# Revit family: 01-70-035-DN100-150
name_source: partatom
category: Pipe Accessories
units: mm (PartAtom-declared; Revit-internal decimal feet)

## family parameters
Always vertical = No
Cut with Voids When Loaded = No
Part Type = Valve - Breaks Into
Round Connector Dimension = Use Diameter
Shared = No
Work Plane-Based = No

## types (5) — shared parameters
Body_Wallthickness = 10 mm  [stored 0.0328084 ft]
Body_Wallthickness_1 = 20 mm  [stored 0.0656168 ft]
Body_Wallthickness_2 = 5 mm  [stored 0.0164042 ft]
Bonnet_Flange_cut = 8 mm  [stored 0.0262467 ft]
Bonnet_Flange_thickness = 15 mm  [stored 0.0492126 ft]
D = 63 mm  [stored 0.206693 ft]
D1 = 10 mm  [stored 0.0328084 ft]
D2 = 34 mm  [stored 0.111549 ft]
DN100_PN16 = 01-110-70-0146499
DN125_PN 16 = 01-140-70-0146499
DN125_PN16 = 01-125-70-0146499
DN150_PN 16 = 01-160-70-0146499
DN150_PN16 = 01-180-70-0146499
Description_ = AVK GATE VALVE, SUPA PLUS™
E = 15 mm  [stored 0.0492126 ft]
F = 10 mm  [stored 0.0328084 ft]
F1 = 22 mm  [stored 0.0721785 ft]
Flange_Thickness = 19 mm  [stored 0.062336 ft]
Flange_width = 30 mm  [stored 0.0984252 ft]
Ftc = 4 mm  [stored 0.0131234 ft]
Name_Height_reference = 10 mm  [stored 0.0328084 ft]
Rib_Height_Reference_1 = 120 mm
Rib_Height_Reference_2 = 110 mm
Rib_Height_Reference_3 = 100 mm
Rib_Thickness = 18 mm  [stored 0.0590551 ft]
Search_table = 01-70-035-DN100-150
URL product pages = https://www.avkvalves.com
zero-valued in all types: Bottom_Reference

## per-type parameters (varying)
- DN100_PN16: At=83 mm; Body_Height=122 mm; Body_depth=166 mm; Body_width=80 mm  [stored 0.262467 ft]; Bonnet_Flange_Depth=192 mm; Bonnet_Flange_Width=81 mm  [stored 0.265748 ft]; Bonnet_Height=55 mm  [stored 0.180446 ft]; Bonnet_Reference_height=112 mm; Bonnet_Thickness=82 mm; Bt=82 mm; Bt_2=74 mm  [stored 0.242782 ft]; CL _Thickness=29 mm  [stored 0.0951444 ft]; CL_Height=88 mm; Cut_Reference=660 mm; Dd=110 mm; Dd_ref=75 mm; Dd_ref_1=55 mm  [stored 0.180446 ft]; Fillet_Thickness=6 mm  [stored 0.019685 ft]; Flange_OR=110 mm; Flange_Thickness_cut=30 mm  [stored 0.0984252 ft]; Flange_depth=192 mm; Ftc_reference_height=110 mm; H=305 mm; H1=271 mm; H2=90 mm; H3=395 mm; Horizontal_Flange_width=180 mm; ID (Radius)=50 mm  [stored 0.164042 ft]; L=330 mm; L1=229 mm; L2=72 mm  [stored 0.23622 ft]; L_Dia=100 mm; L_ref=280 mm; Name_Reference=101 mm; Name_Width=40 mm  [stored 0.131234 ft]; Neck_H=61 mm; Neck_T=27 mm  [stored 0.0885827 ft]; Neck_T2=25 mm  [stored 0.082021 ft]; Nominal Diameter (DN)=100 mm; OD=66 mm  [stored 0.216535 ft]; R1tv=1100 mm; R2f=15 mm  [stored 0.0492126 ft]; RF_Dia=78 mm  [stored 0.255906 ft]; Rf=300 mm; Rib_Height_Reference_4=90 mm; Rib_Width_1=40 mm  [stored 0.131234 ft]; Rib_Width_2=40 mm  [stored 0.131234 ft]; Rib_Width_3=40 mm  [stored 0.131234 ft]; Rib_depth_1=40 mm  [stored 0.131234 ft]; Rib_depth_2=40 mm  [stored 0.131234 ft]; Rib_depth_3=40 mm  [stored 0.131234 ft]; Rt=367 mm
- DN125_PN16: At=97 mm; Body_Height=137 mm; Body_depth=194 mm; Body_width=90 mm; Bonnet_Flange_Depth=220 mm; Bonnet_Flange_Width=83 mm; Bonnet_Height=63 mm  [stored 0.206693 ft]; Bonnet_Reference_height=127 mm; Bonnet_Thickness=92 mm; Bt=92 mm; Bt_2=84 mm; CL _Thickness=34 mm  [stored 0.111549 ft]; CL_Height=102 mm; Cut_Reference=712 mm; Dd=140 mm; Dd_ref=90 mm; Dd_ref_1=70 mm  [stored 0.229659 ft]; Fillet_Thickness=6 mm  [stored 0.019685 ft]; Flange_OR=125 mm; Flange_Thickness_cut=31 mm; Flange_depth=220 mm; Ftc_reference_height=125 mm; H=352 mm; H1=318 mm; H2=106 mm; H3=458 mm; Horizontal_Flange_width=212 mm; ID (Radius)=63 mm  [stored 0.206693 ft]; L=356 mm; L1=229 mm; L2=80 mm  [stored 0.262467 ft]; L_Dia=125 mm; L_ref=293 mm; Name_Reference=114 mm; Name_Width=45 mm  [stored 0.147638 ft]; Neck_H=79 mm; Neck_T=32 mm  [stored 0.104987 ft]; Neck_T2=30 mm  [stored 0.0984252 ft]; Nominal Diameter (DN)=125 mm; OD=76 mm; R1tv=1250 mm; R2f=15 mm  [stored 0.0492126 ft]; RF_Dia=92 mm; Rf=353 mm; Rib_Height_Reference_4=120 mm; Rib_Width_1=45 mm  [stored 0.147638 ft]; Rib_Width_2=45 mm  [stored 0.147638 ft]; Rib_Width_3=45 mm  [stored 0.147638 ft]; Rib_depth_1=45 mm  [stored 0.147638 ft]; Rib_depth_2=45 mm  [stored 0.147638 ft]; Rib_depth_3=45 mm  [stored 0.147638 ft]; Rt=417 mm
- DN125_PN 16: At=97 mm; Body_Height=137 mm; Body_depth=194 mm; Body_width=90 mm; Bonnet_Flange_Depth=220 mm; Bonnet_Flange_Width=83 mm; Bonnet_Height=63 mm  [stored 0.206693 ft]; Bonnet_Reference_height=127 mm; Bonnet_Thickness=92 mm; Bt=92 mm; Bt_2=84 mm; CL _Thickness=34 mm  [stored 0.111549 ft]; CL_Height=102 mm; Cut_Reference=674 mm; Dd=125 mm; Dd_ref=83 mm; Dd_ref_1=63 mm  [stored 0.206693 ft]; Fillet_Thickness=6 mm  [stored 0.019685 ft]; Flange_OR=125 mm; Flange_Thickness_cut=31 mm; Flange_depth=220 mm; Ftc_reference_height=125 mm; H=352 mm; H1=318 mm; H2=100 mm; H3=452 mm; Horizontal_Flange_width=200 mm; ID (Radius)=63 mm  [stored 0.206693 ft]; L=337 mm; L1=229 mm; L2=80 mm  [stored 0.262467 ft]; L_Dia=125 mm; L_ref=283 mm; Name_Reference=114 mm; Name_Width=45 mm  [stored 0.147638 ft]; Neck_H=79 mm; Neck_T=32 mm  [stored 0.104987 ft]; Neck_T2=30 mm  [stored 0.0984252 ft]; Nominal Diameter (DN)=125 mm; OD=76 mm; R1tv=1250 mm; R2f=15 mm  [stored 0.0492126 ft]; RF_Dia=92 mm; Rf=333 mm; Rib_Height_Reference_4=120 mm; Rib_Width_1=45 mm  [stored 0.147638 ft]; Rib_Width_2=45 mm  [stored 0.147638 ft]; Rib_Width_3=45 mm  [stored 0.147638 ft]; Rib_depth_1=45 mm  [stored 0.147638 ft]; Rib_depth_2=45 mm  [stored 0.147638 ft]; Rib_depth_3=45 mm  [stored 0.147638 ft]; Rt=417 mm
- DN150_PN 16: At=121 mm; Body_Height=172 mm; Body_depth=242 mm; Body_width=95 mm; Bonnet_Flange_Depth=272 mm; Bonnet_Flange_Width=116 mm; Bonnet_Height=71 mm  [stored 0.23294 ft]; Bonnet_Reference_height=162 mm; Bonnet_Thickness=97 mm; Bt=97 mm; Bt_2=89 mm; CL _Thickness=34 mm  [stored 0.111549 ft]; CL_Height=126 mm; Cut_Reference=742 mm; Dd=160 mm; Dd_ref=100 mm; Dd_ref_1=80 mm  [stored 0.262467 ft]; Fillet_Thickness=12 mm  [stored 0.0393701 ft]; Flange_OR=142 mm; Flange_Thickness_cut=34 mm  [stored 0.111549 ft]; Flange_depth=272 mm; Ftc_reference_height=142 mm; H=400 mm; H1=366 mm; H2=117 mm; H3=517 mm; Horizontal_Flange_width=234 mm; ID (Radius)=75 mm; L=371 mm; L1=249 mm; L2=99 mm; L_Dia=150 mm; L_ref=310 mm; Name_Reference=143 mm; Name_Width=48 mm  [stored 0.15748 ft]; Neck_H=68 mm; Neck_T=32 mm  [stored 0.104987 ft]; Neck_T2=30 mm  [stored 0.0984252 ft]; Nominal Diameter (DN)=150 mm; OD=93 mm; R1tv=1420 mm; R2f=30 mm  [stored 0.0984252 ft]; RF_Dia=106 mm; Rf=390 mm; Rib_Height_Reference_4=150 mm; Rib_Width_1=48 mm  [stored 0.15748 ft]; Rib_Width_2=48 mm  [stored 0.15748 ft]; Rib_Width_3=48 mm  [stored 0.15748 ft]; Rib_depth_1=48 mm  [stored 0.15748 ft]; Rib_depth_2=48 mm  [stored 0.15748 ft]; Rib_depth_3=48 mm  [stored 0.15748 ft]; Rt=473 mm
- DN150_PN16: At=121 mm; Body_Height=172 mm; Body_depth=242 mm; Body_width=95 mm; Bonnet_Flange_Depth=272 mm; Bonnet_Flange_Width=116 mm; Bonnet_Height=71 mm  [stored 0.23294 ft]; Bonnet_Reference_height=162 mm; Bonnet_Thickness=97 mm; Bt=97 mm; Bt_2=89 mm; CL _Thickness=34 mm  [stored 0.111549 ft]; CL_Height=126 mm; Cut_Reference=798 mm; Dd=180 mm; Dd_ref=110 mm; Dd_ref_1=90 mm; Fillet_Thickness=12 mm  [stored 0.0393701 ft]; Flange_OR=142 mm; Flange_Thickness_cut=33 mm; Flange_depth=272 mm; Ftc_reference_height=142 mm; H=400 mm; H1=366 mm; H2=125 mm; H3=525 mm; Horizontal_Flange_width=250 mm; ID (Radius)=75 mm; L=399 mm; L1=249 mm; L2=99 mm; L_Dia=150 mm; L_ref=324 mm; Name_Reference=143 mm; Name_Width=48 mm  [stored 0.15748 ft]; Neck_H=68 mm; Neck_T=32 mm  [stored 0.104987 ft]; Neck_T2=30 mm  [stored 0.0984252 ft]; Nominal Diameter (DN)=150 mm; OD=103 mm; R1tv=1420 mm; R2f=30 mm  [stored 0.0984252 ft]; RF_Dia=106 mm; Rf=417 mm; Rib_Height_Reference_4=150 mm; Rib_Width_1=48 mm  [stored 0.15748 ft]; Rib_Width_2=48 mm  [stored 0.15748 ft]; Rib_Width_3=48 mm  [stored 0.15748 ft]; Rib_depth_1=48 mm  [stored 0.15748 ft]; Rib_depth_2=48 mm  [stored 0.15748 ft]; Rib_depth_3=48 mm  [stored 0.15748 ft]; Rt=473 mm

note: [stored X ft] marks values corroborated as IEEE doubles in the binary element streams (Revit-internal decimal feet)

## geometry (parser evidence)
native form markers: Sweep x2
no freeform markers — native parametric forms only
